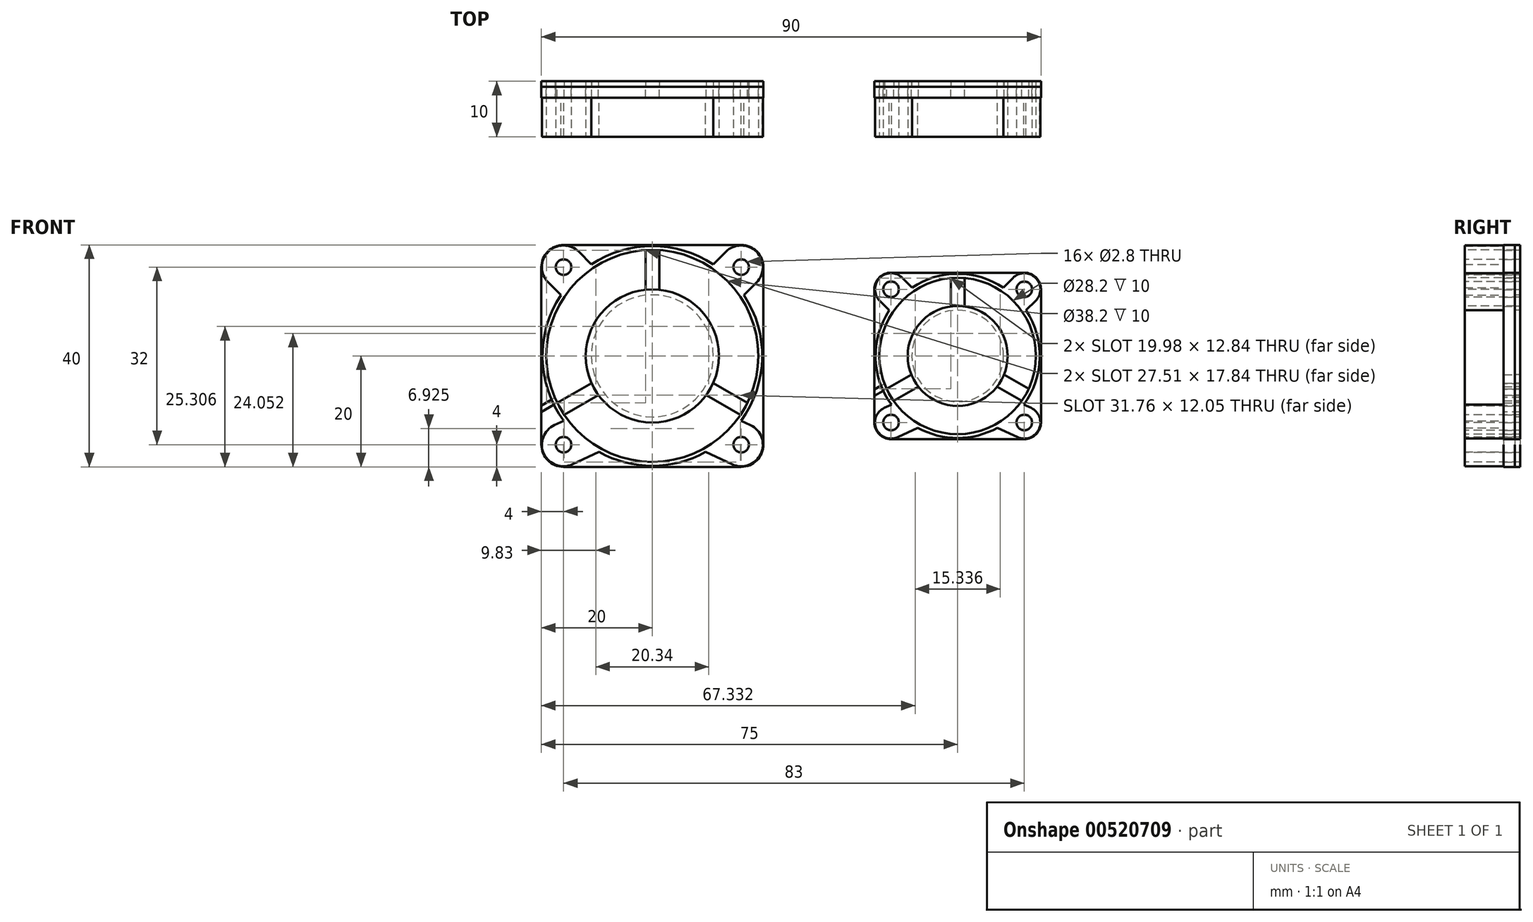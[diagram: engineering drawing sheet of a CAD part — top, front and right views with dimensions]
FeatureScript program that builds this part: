
annotation { "Feature Type Name" : "Feature", "Feature Type Description" : "" }
export const myFeature = defineFeature(function(context is Context, id is Id, definition is map)
    precondition{}
    {
        {
            assignVariable(context, id + "F0", {"name" : "height", "anyValue" : 10 * mm});
        }
        {
            assignVariable(context, id + "F1", {"name" : "lvl1_height", "anyValue" : 1 * mm});
        }
        {
            assignVariable(context, id + "F2", {"name" : "lvl2_height", "anyValue" : 2 * mm});
        }
        {
            var Q0;
            Q0=qCreatedBy(makeId("Front.planeOp"),FACE);
            var sketch = newSketch(context, id + "F3", { "sketchPlane" : qUnion([Q0])});
            skLineSegment(sketch, "E0", {"start": v(0, 0) * mm, "end": v(-30, 0) * mm, "construction": true});
            skLineSegment(sketch, "E1", {"start": v(0, 0) * mm, "end": v(25, 0) * mm, "construction": true});
            skCircle(sketch, "E2", {"center": v(-30, 0) * mm, "radius": 11 * mm});
            skCircle(sketch, "E3", {"center": v(25, 0) * mm, "radius": 8.25 * mm});
            skCircle(sketch, "E4", {"center": v(-30, 0) * mm, "radius": 12 * mm});
            skCircle(sketch, "E5", {"center": v(25, 0) * mm, "radius": 9 * mm});
            skCircle(sketch, "E6", {"center": v(-30, 0) * mm, "radius": 19.1 * mm});
            skCircle(sketch, "E7", {"center": v(25, 0) * mm, "radius": 14.1 * mm});
            skCircle(sketch, "E8", {"center": v(-30, 0) * mm, "radius": 19.8 * mm});
            skCircle(sketch, "E9", {"center": v(25, 0) * mm, "radius": 14.8 * mm});
            skLineSegment(sketch, "E10", {"start": v(-30, 0) * mm, "end": v(-28.75, 0) * mm, "construction": true});
            skLineSegment(sketch, "E11", {"start": v(-28.75, 0) * mm, "end": v(-28.75, 10.93) * mm, "construction": true});
            skLineSegment(sketch, "E12", {"start": v(-28.75, 10.93) * mm, "end": v(-28.75, 19.06) * mm});
            skLineSegment(sketch, "E13", {"start": v(-30, 0) * mm, "end": v(-30, 25) * mm, "construction": true});
            skLineSegment(sketch, "E14.MirrorCS", {"start": v(-31.25, 10.93) * mm, "end": v(-31.25, 19.06) * mm});
            skLineSegment(sketch, "E15.1.0", {"start": v(-40.09, -4.38) * mm, "end": v(-47.13, -8.45) * mm});
            skLineSegment(sketch, "E15.1.1", {"start": v(-38.84, -6.55) * mm, "end": v(-45.88, -10.61) * mm});
            skLineSegment(sketch, "E15.2.0", {"start": v(-21.16, -6.55) * mm, "end": v(-14.12, -10.61) * mm});
            skLineSegment(sketch, "E15.2.1", {"start": v(-19.91, -4.38) * mm, "end": v(-12.87, -8.45) * mm});
            skLineSegment(sketch, "E16", {"start": v(25, 0) * mm, "end": v(26.25, 0) * mm, "construction": true});
            skLineSegment(sketch, "E17", {"start": v(26.25, 0) * mm, "end": v(26.25, 8.15) * mm, "construction": true});
            skLineSegment(sketch, "E18", {"start": v(26.25, 8.15) * mm, "end": v(26.25, 14.04) * mm});
            skLineSegment(sketch, "E19", {"start": v(25, 0) * mm, "end": v(25, 20) * mm, "construction": true});
            skLineSegment(sketch, "E20.MirrorCS", {"start": v(23.75, 8.15) * mm, "end": v(23.75, 14.04) * mm});
            skLineSegment(sketch, "E21.1.0", {"start": v(17.31, -3) * mm, "end": v(12.21, -5.94) * mm});
            skLineSegment(sketch, "E21.1.1", {"start": v(18.56, -5.16) * mm, "end": v(13.46, -8.1) * mm});
            skLineSegment(sketch, "E21.2.0", {"start": v(31.44, -5.16) * mm, "end": v(36.54, -8.1) * mm});
            skLineSegment(sketch, "E21.2.1", {"start": v(32.69, -3) * mm, "end": v(37.79, -5.94) * mm});
            skLineSegment(sketch, "E22", {"start": v(-30, 0) * mm, "end": v(-46, 0) * mm, "construction": true});
            skLineSegment(sketch, "E23", {"start": v(-46, 0) * mm, "end": v(-46, 16) * mm, "construction": true});
            skCircle(sketch, "E24", {"center": v(-46, 16) * mm, "radius": 1.4 * mm});
            skCircle(sketch, "E25.1.0", {"center": v(-46, -16) * mm, "radius": 1.4 * mm});
            skCircle(sketch, "E25.2.0", {"center": v(-14, -16) * mm, "radius": 1.4 * mm});
            skCircle(sketch, "E25.3.0", {"center": v(-14, 16) * mm, "radius": 1.4 * mm});
            skLineSegment(sketch, "E26", {"start": v(25, 0) * mm, "end": v(13, 0) * mm, "construction": true});
            skLineSegment(sketch, "E27", {"start": v(13, 0) * mm, "end": v(13, 12) * mm, "construction": true});
            skCircle(sketch, "E28", {"center": v(13, 12) * mm, "radius": 1.4 * mm});
            skCircle(sketch, "E29.1.0", {"center": v(13, -12) * mm, "radius": 1.4 * mm});
            skCircle(sketch, "E29.2.0", {"center": v(37, -12) * mm, "radius": 1.4 * mm});
            skCircle(sketch, "E29.3.0", {"center": v(37, 12) * mm, "radius": 1.4 * mm});
            skLineSegment(sketch, "E30", {"start": v(-30, 20) * mm, "end": v(-46, 20) * mm});
            skLineSegment(sketch, "E31", {"start": v(-50, 16) * mm, "end": v(-50, 0) * mm});
            skPoint(sketch, "E32.visualSharp", {"position": v(-50, 20) * mm});
            skArc(sketch, "E32.filletArc", {"start": v(-46, 20) * mm, "mid": v(-48.83, 18.83) * mm, "end": v(-50, 16) * mm});
            skLineSegment(sketch, "E33.MirrorCS", {"start": v(-30, 20) * mm, "end": v(-14, 20) * mm});
            skLineSegment(sketch, "E34.MirrorCS", {"start": v(-10, 16) * mm, "end": v(-10, 0) * mm});
            skArc(sketch, "E35.MirrorCS", {"start": v(-14, 20) * mm, "mid": v(-11.17, 18.83) * mm, "end": v(-10, 16) * mm});
            skLineSegment(sketch, "E36.MirrorCS", {"start": v(-50, -16) * mm, "end": v(-50, 0) * mm});
            skArc(sketch, "E37.MirrorCS", {"start": v(-46, -20) * mm, "mid": v(-48.83, -18.83) * mm, "end": v(-50, -16) * mm});
            skLineSegment(sketch, "E38.MirrorCS", {"start": v(-30, -20) * mm, "end": v(-46, -20) * mm});
            skLineSegment(sketch, "E39.MirrorCS", {"start": v(-10, -16) * mm, "end": v(-10, 0) * mm});
            skLineSegment(sketch, "E40.MirrorCS", {"start": v(-30, -20) * mm, "end": v(-14, -20) * mm});
            skArc(sketch, "E41.MirrorCS", {"start": v(-14, -20) * mm, "mid": v(-11.17, -18.83) * mm, "end": v(-10, -16) * mm});
            skLineSegment(sketch, "E42", {"start": v(25, 15) * mm, "end": v(13, 15) * mm});
            skLineSegment(sketch, "E43", {"start": v(10, 12) * mm, "end": v(10, 0) * mm});
            skPoint(sketch, "E44.visualSharp", {"position": v(10, 15) * mm});
            skArc(sketch, "E44.filletArc", {"start": v(13, 15) * mm, "mid": v(10.88, 14.12) * mm, "end": v(10, 12) * mm});
            skLineSegment(sketch, "E45.MirrorCS", {"start": v(25, 15) * mm, "end": v(37, 15) * mm});
            skLineSegment(sketch, "E46.MirrorCS", {"start": v(40, 12) * mm, "end": v(40, 0) * mm});
            skArc(sketch, "E47.MirrorCS", {"start": v(37, 15) * mm, "mid": v(39.12, 14.12) * mm, "end": v(40, 12) * mm});
            skLineSegment(sketch, "E48.MirrorCS", {"start": v(10, -12) * mm, "end": v(10, 0) * mm});
            skArc(sketch, "E49.MirrorCS", {"start": v(13, -15) * mm, "mid": v(10.88, -14.12) * mm, "end": v(10, -12) * mm});
            skLineSegment(sketch, "E50.MirrorCS", {"start": v(25, -15) * mm, "end": v(13, -15) * mm});
            skLineSegment(sketch, "E51.MirrorCS", {"start": v(40, -12) * mm, "end": v(40, 0) * mm});
            skLineSegment(sketch, "E52.MirrorCS", {"start": v(25, -15) * mm, "end": v(37, -15) * mm});
            skArc(sketch, "E53.MirrorCS", {"start": v(37, -15) * mm, "mid": v(39.12, -14.12) * mm, "end": v(40, -12) * mm});
            skLineSegment(sketch, "E54", {"start": v(-40.97, 16.48) * mm, "end": v(-43.24, 18.76) * mm});
            skLineSegment(sketch, "E55", {"start": v(-46.48, 10.97) * mm, "end": v(-48.76, 13.24) * mm});
            skArc(sketch, "E56", {"start": v(-43.24, 18.76) * mm, "mid": v(-48.76, 18.76) * mm, "end": v(-48.76, 13.24) * mm});
            skLineSegment(sketch, "E57.MirrorCS", {"start": v(-19.03, 16.48) * mm, "end": v(-16.76, 18.76) * mm});
            skLineSegment(sketch, "E58.MirrorCS", {"start": v(-13.52, 10.97) * mm, "end": v(-11.24, 13.24) * mm});
            skArc(sketch, "E59.MirrorCS", {"start": v(-16.76, 18.76) * mm, "mid": v(-11.24, 18.76) * mm, "end": v(-11.24, 13.24) * mm});
            skLineSegment(sketch, "E60", {"start": v(-47.7, -12.37) * mm, "end": v(-46, -16) * mm, "construction": true});
            skLineSegment(sketch, "E61", {"start": v(-46, -16) * mm, "end": v(-44.13, -20) * mm, "construction": true});
            skArc(sketch, "E62", {"start": v(-44.35, -19.53) * mm, "mid": v(-49.53, -17.65) * mm, "end": v(-47.65, -12.47) * mm});
            skLineSegment(sketch, "E63", {"start": v(-44.35, -19.53) * mm, "end": v(-39.6, -17.32) * mm});
            skLineSegment(sketch, "E64", {"start": v(-47.65, -12.47) * mm, "end": v(-45.98, -11.69) * mm});
            skLineSegment(sketch, "E65.MirrorCS", {"start": v(-12.35, -12.47) * mm, "end": v(-14.02, -11.69) * mm});
            skLineSegment(sketch, "E66.MirrorCS", {"start": v(-15.65, -19.53) * mm, "end": v(-20.4, -17.32) * mm});
            skArc(sketch, "E67.MirrorCS", {"start": v(-15.65, -19.53) * mm, "mid": v(-10.47, -17.65) * mm, "end": v(-12.35, -12.47) * mm});
            skLineSegment(sketch, "E68", {"start": v(-47.13, -8.45) * mm, "end": v(-50, -10.1) * mm});
            skLineSegment(sketch, "E69", {"start": v(-47.55, -7.53) * mm, "end": v(-50, -8.95) * mm});
            skLineSegment(sketch, "E70", {"start": v(15.12, 14.12) * mm, "end": v(13, 12) * mm, "construction": true});
            skLineSegment(sketch, "E71", {"start": v(13, 12) * mm, "end": v(10.88, 9.88) * mm, "construction": true});
            skArc(sketch, "E72", {"start": v(15.05, 14.05) * mm, "mid": v(10.95, 14.05) * mm, "end": v(10.95, 9.95) * mm});
            skLineSegment(sketch, "E73", {"start": v(15.05, 14.05) * mm, "end": v(16.79, 12.31) * mm});
            skLineSegment(sketch, "E74", {"start": v(10.95, 9.95) * mm, "end": v(12.69, 8.21) * mm});
            skLineSegment(sketch, "E75", {"start": v(11.73, -9.28) * mm, "end": v(13, -12) * mm, "construction": true});
            skLineSegment(sketch, "E76", {"start": v(13, -12) * mm, "end": v(14.27, -14.72) * mm, "construction": true});
            skArc(sketch, "E77", {"start": v(11.77, -9.37) * mm, "mid": v(10.37, -13.23) * mm, "end": v(14.23, -14.63) * mm});
            skLineSegment(sketch, "E78", {"start": v(11.77, -9.37) * mm, "end": v(13.07, -8.77) * mm});
            skLineSegment(sketch, "E79", {"start": v(14.23, -14.63) * mm, "end": v(17.83, -12.95) * mm});
            skArc(sketch, "E80.MirrorCS", {"start": v(38.23, -9.37) * mm, "mid": v(39.63, -13.23) * mm, "end": v(35.77, -14.63) * mm});
            skLineSegment(sketch, "E81.MirrorCS", {"start": v(35.77, -14.63) * mm, "end": v(32.17, -12.95) * mm});
            skLineSegment(sketch, "E82.MirrorCS", {"start": v(38.23, -9.37) * mm, "end": v(36.93, -8.77) * mm});
            skLineSegment(sketch, "E83.MirrorCS", {"start": v(34.95, 14.05) * mm, "end": v(33.21, 12.31) * mm});
            skLineSegment(sketch, "E84.MirrorCS", {"start": v(39.05, 9.95) * mm, "end": v(37.31, 8.21) * mm});
            skArc(sketch, "E85.MirrorCS", {"start": v(34.95, 14.05) * mm, "mid": v(39.05, 14.05) * mm, "end": v(39.05, 9.95) * mm});
            skLineSegment(sketch, "E86", {"start": v(12.21, -5.94) * mm, "end": v(10, -7.22) * mm});
            skLineSegment(sketch, "E87", {"start": v(11.82, -5.01) * mm, "end": v(10, -6.06) * mm});
            skSolve(sketch);
        }
        {
            var Q0;
            Q0=makeQuery(id+"F3.imprint","IMPRINT",FACE,{"disambiguationData":[TD([[makeQuery(id+"F3.imprint","IMPRINT",EDGE,{"derivedFrom":sQuery(id+"F3.wireOp",EDGE,"E25.3.0")}),-1.0]])]});
            var Q1;
            Q1=makeQuery(id+"F3.imprint","IMPRINT",FACE,{"disambiguationData":[TD([[makeQuery(id+"F3.imprint","IMPRINT",EDGE,{"derivedFrom":sQuery(id+"F3.wireOp",EDGE,"E30")}),1.0]])]});
            var Q2;
            {var subQ4=sQuery(id+"F3.wireOp",EDGE,"E6");var subQ5=makeQuery(id+"F3.imprint","INTERSECT",VERTEX,{"derivedFrom":[subQ4,sQuery(id+"F3.wireOp",EDGE,"E12")]});Q2=makeQuery(id+"F3.imprint","IMPRINT",FACE,{"disambiguationData":[TD([[makeQuery(id+"F3.imprint","IMPRINT",EDGE,{"disambiguationData":[TD([[subQ5,-1.0]])],"derivedFrom":subQ4}),-1.0]])]});}
            var Q3;
            Q3=makeQuery(id+"F3.imprint","IMPRINT",FACE,{"disambiguationData":[TD([[makeQuery(id+"F3.imprint","IMPRINT",EDGE,{"derivedFrom":sQuery(id+"F3.wireOp",EDGE,"E24")}),-1.0]])]});
            var Q4;
            Q4=makeQuery(id+"F3.imprint","IMPRINT",FACE,{"disambiguationData":[TD([[makeQuery(id+"F3.imprint","IMPRINT",EDGE,{"derivedFrom":sQuery(id+"F3.wireOp",EDGE,"E25.1.0")}),-1.0]])]});
            var Q5;
            Q5=makeQuery(id+"F3.imprint","IMPRINT",FACE,{"disambiguationData":[TD([[makeQuery(id+"F3.imprint","IMPRINT",EDGE,{"derivedFrom":sQuery(id+"F3.wireOp",EDGE,"E25.2.0")}),-1.0]])]});
            var Q6;
            Q6=makeQuery(id+"F3.imprint","IMPRINT",FACE,{"disambiguationData":[TD([[makeQuery(id+"F3.imprint","IMPRINT",EDGE,{"derivedFrom":sQuery(id+"F3.wireOp",EDGE,"E29.2.0")}),-1.0]])]});
            var Q7;
            Q7=makeQuery(id+"F3.imprint","IMPRINT",FACE,{"disambiguationData":[TD([[makeQuery(id+"F3.imprint","IMPRINT",EDGE,{"derivedFrom":sQuery(id+"F3.wireOp",EDGE,"E42")}),1.0]])]});
            var Q8;
            Q8=makeQuery(id+"F3.imprint","IMPRINT",FACE,{"disambiguationData":[TD([[makeQuery(id+"F3.imprint","IMPRINT",EDGE,{"derivedFrom":sQuery(id+"F3.wireOp",EDGE,"E29.1.0")}),-1.0]])]});
            var Q9;
            Q9=makeQuery(id+"F3.imprint","IMPRINT",FACE,{"disambiguationData":[TD([[makeQuery(id+"F3.imprint","IMPRINT",EDGE,{"derivedFrom":sQuery(id+"F3.wireOp",EDGE,"E28")}),-1.0]])]});
            var Q10;
            Q10=makeQuery(id+"F3.imprint","IMPRINT",FACE,{"disambiguationData":[TD([[makeQuery(id+"F3.imprint","IMPRINT",EDGE,{"derivedFrom":sQuery(id+"F3.wireOp",EDGE,"E29.3.0")}),-1.0]])]});
            var Q11;
            {var subQ7=sQuery(id+"F3.wireOp",EDGE,"E7");var subQ8=makeQuery(id+"F3.imprint","INTERSECT",VERTEX,{"derivedFrom":[subQ7,sQuery(id+"F3.wireOp",EDGE,"E18")]});Q11=makeQuery(id+"F3.imprint","IMPRINT",FACE,{"disambiguationData":[TD([[makeQuery(id+"F3.imprint","IMPRINT",EDGE,{"disambiguationData":[TD([[subQ8,-1.0]])],"derivedFrom":subQ7}),-1.0]])]});}
            var Q12;
            {var subQ0=sQuery(id+"F3.wireOp",EDGE,"E15.2.0");var subQ1=sQuery(id+"F3.wireOp",EDGE,"E4");var subQ2=makeQuery(id+"F3.imprint","INTERSECT",VERTEX,{"derivedFrom":[subQ1,subQ0]});Q12=makeQuery(id+"F3.imprint","IMPRINT",FACE,{"disambiguationData":[TD([[makeQuery(id+"F3.imprint","IMPRINT",EDGE,{"disambiguationData":[TD([[subQ2,-1.0]])],"derivedFrom":subQ1}),-1.0]])]});}
            var Q13;
            {var subQ0=sQuery(id+"F3.wireOp",EDGE,"E15.1.0");var subQ1=sQuery(id+"F3.wireOp",EDGE,"E4");var subQ2=makeQuery(id+"F3.imprint","INTERSECT",VERTEX,{"derivedFrom":[subQ1,subQ0]});Q13=makeQuery(id+"F3.imprint","IMPRINT",FACE,{"disambiguationData":[TD([[makeQuery(id+"F3.imprint","IMPRINT",EDGE,{"disambiguationData":[TD([[subQ2,-1.0]])],"derivedFrom":subQ1}),-1.0]])]});}
            var Q14;
            {var subQ0=sQuery(id+"F3.wireOp",EDGE,"E14.MirrorCS");var subQ1=sQuery(id+"F3.wireOp",EDGE,"E4");var subQ2=makeQuery(id+"F3.imprint","INTERSECT",VERTEX,{"derivedFrom":[subQ1,subQ0]});Q14=makeQuery(id+"F3.imprint","IMPRINT",FACE,{"disambiguationData":[TD([[makeQuery(id+"F3.imprint","IMPRINT",EDGE,{"disambiguationData":[TD([[subQ2,1.0]])],"derivedFrom":subQ1}),-1.0]])]});}
            var Q15;
            {var subQ0=sQuery(id+"F3.wireOp",EDGE,"E12");var subQ1=sQuery(id+"F3.wireOp",EDGE,"E2");var subQ2=makeQuery(id+"F3.imprint","INTERSECT",VERTEX,{"derivedFrom":[subQ1,subQ0]});Q15=makeQuery(id+"F3.imprint","IMPRINT",FACE,{"disambiguationData":[TD([[makeQuery(id+"F3.imprint","IMPRINT",EDGE,{"disambiguationData":[TD([[subQ2,1.0]])],"derivedFrom":subQ1}),-1.0]])]});}
            var Q16;
            {var subQ0=sQuery(id+"F3.wireOp",EDGE,"E15.2.0");var subQ1=sQuery(id+"F3.wireOp",EDGE,"E2");var subQ2=makeQuery(id+"F3.imprint","INTERSECT",VERTEX,{"derivedFrom":[subQ1,subQ0]});Q16=makeQuery(id+"F3.imprint","IMPRINT",FACE,{"disambiguationData":[TD([[makeQuery(id+"F3.imprint","IMPRINT",EDGE,{"disambiguationData":[TD([[subQ2,-1.0]])],"derivedFrom":subQ1}),-1.0]])]});}
            var Q17;
            {var subQ0=sQuery(id+"F3.wireOp",EDGE,"E15.1.1");var subQ1=sQuery(id+"F3.wireOp",EDGE,"E2");var subQ2=makeQuery(id+"F3.imprint","INTERSECT",VERTEX,{"derivedFrom":[subQ1,subQ0]});Q17=makeQuery(id+"F3.imprint","IMPRINT",FACE,{"disambiguationData":[TD([[makeQuery(id+"F3.imprint","IMPRINT",EDGE,{"disambiguationData":[TD([[subQ2,-1.0]])],"derivedFrom":subQ1}),-1.0]])]});}
            var Q18;
            {var subQ0=sQuery(id+"F3.wireOp",EDGE,"E14.MirrorCS");var subQ1=sQuery(id+"F3.wireOp",EDGE,"E2");var subQ2=makeQuery(id+"F3.imprint","INTERSECT",VERTEX,{"derivedFrom":[subQ1,subQ0]});Q18=makeQuery(id+"F3.imprint","IMPRINT",FACE,{"disambiguationData":[TD([[makeQuery(id+"F3.imprint","IMPRINT",EDGE,{"disambiguationData":[TD([[subQ2,-1.0]])],"derivedFrom":subQ1}),-1.0]])]});}
            var Q19;
            {var subQ0=sQuery(id+"F3.wireOp",EDGE,"E15.1.0");var subQ1=sQuery(id+"F3.wireOp",EDGE,"E2");var subQ2=makeQuery(id+"F3.imprint","INTERSECT",VERTEX,{"derivedFrom":[subQ1,subQ0]});Q19=makeQuery(id+"F3.imprint","IMPRINT",FACE,{"disambiguationData":[TD([[makeQuery(id+"F3.imprint","IMPRINT",EDGE,{"disambiguationData":[TD([[subQ2,-1.0]])],"derivedFrom":subQ1}),-1.0]])]});}
            var Q20;
            {var subQ0=sQuery(id+"F3.wireOp",EDGE,"E12");var subQ1=sQuery(id+"F3.wireOp",EDGE,"E2");var subQ2=makeQuery(id+"F3.imprint","INTERSECT",VERTEX,{"derivedFrom":[subQ1,subQ0]});Q20=makeQuery(id+"F3.imprint","IMPRINT",FACE,{"disambiguationData":[TD([[makeQuery(id+"F3.imprint","IMPRINT",EDGE,{"disambiguationData":[TD([[subQ2,-1.0]])],"derivedFrom":subQ1}),-1.0]])]});}
            var Q21;
            {var subQ0=sQuery(id+"F3.wireOp",EDGE,"E21.2.0");var subQ1=sQuery(id+"F3.wireOp",EDGE,"E5");var subQ2=makeQuery(id+"F3.imprint","INTERSECT",VERTEX,{"derivedFrom":[subQ1,subQ0]});Q21=makeQuery(id+"F3.imprint","IMPRINT",FACE,{"disambiguationData":[TD([[makeQuery(id+"F3.imprint","IMPRINT",EDGE,{"disambiguationData":[TD([[subQ2,-1.0]])],"derivedFrom":subQ1}),-1.0]])]});}
            var Q22;
            {var subQ0=sQuery(id+"F3.wireOp",EDGE,"E21.1.0");var subQ1=sQuery(id+"F3.wireOp",EDGE,"E5");var subQ2=makeQuery(id+"F3.imprint","INTERSECT",VERTEX,{"derivedFrom":[subQ1,subQ0]});Q22=makeQuery(id+"F3.imprint","IMPRINT",FACE,{"disambiguationData":[TD([[makeQuery(id+"F3.imprint","IMPRINT",EDGE,{"disambiguationData":[TD([[subQ2,-1.0]])],"derivedFrom":subQ1}),-1.0]])]});}
            var Q23;
            {var subQ0=sQuery(id+"F3.wireOp",EDGE,"E18");var subQ1=sQuery(id+"F3.wireOp",EDGE,"E3");var subQ2=makeQuery(id+"F3.imprint","INTERSECT",VERTEX,{"derivedFrom":[subQ1,subQ0]});Q23=makeQuery(id+"F3.imprint","IMPRINT",FACE,{"disambiguationData":[TD([[makeQuery(id+"F3.imprint","IMPRINT",EDGE,{"disambiguationData":[TD([[subQ2,1.0]])],"derivedFrom":subQ1}),-1.0]])]});}
            var Q24;
            {var subQ0=sQuery(id+"F3.wireOp",EDGE,"E21.2.0");var subQ1=sQuery(id+"F3.wireOp",EDGE,"E3");var subQ2=makeQuery(id+"F3.imprint","INTERSECT",VERTEX,{"derivedFrom":[subQ1,subQ0]});Q24=makeQuery(id+"F3.imprint","IMPRINT",FACE,{"disambiguationData":[TD([[makeQuery(id+"F3.imprint","IMPRINT",EDGE,{"disambiguationData":[TD([[subQ2,-1.0]])],"derivedFrom":subQ1}),-1.0]])]});}
            var Q25;
            {var subQ0=sQuery(id+"F3.wireOp",EDGE,"E21.1.1");var subQ1=sQuery(id+"F3.wireOp",EDGE,"E3");var subQ2=makeQuery(id+"F3.imprint","INTERSECT",VERTEX,{"derivedFrom":[subQ1,subQ0]});Q25=makeQuery(id+"F3.imprint","IMPRINT",FACE,{"disambiguationData":[TD([[makeQuery(id+"F3.imprint","IMPRINT",EDGE,{"disambiguationData":[TD([[subQ2,-1.0]])],"derivedFrom":subQ1}),-1.0]])]});}
            var Q26;
            {var subQ0=sQuery(id+"F3.wireOp",EDGE,"E20.MirrorCS");var subQ1=sQuery(id+"F3.wireOp",EDGE,"E3");var subQ2=makeQuery(id+"F3.imprint","INTERSECT",VERTEX,{"derivedFrom":[subQ1,subQ0]});Q26=makeQuery(id+"F3.imprint","IMPRINT",FACE,{"disambiguationData":[TD([[makeQuery(id+"F3.imprint","IMPRINT",EDGE,{"disambiguationData":[TD([[subQ2,-1.0]])],"derivedFrom":subQ1}),-1.0]])]});}
            var Q27;
            {var subQ0=sQuery(id+"F3.wireOp",EDGE,"E21.1.0");var subQ1=sQuery(id+"F3.wireOp",EDGE,"E3");var subQ2=makeQuery(id+"F3.imprint","INTERSECT",VERTEX,{"derivedFrom":[subQ1,subQ0]});Q27=makeQuery(id+"F3.imprint","IMPRINT",FACE,{"disambiguationData":[TD([[makeQuery(id+"F3.imprint","IMPRINT",EDGE,{"disambiguationData":[TD([[subQ2,-1.0]])],"derivedFrom":subQ1}),-1.0]])]});}
            var Q28;
            {var subQ0=sQuery(id+"F3.wireOp",EDGE,"E18");var subQ1=sQuery(id+"F3.wireOp",EDGE,"E3");var subQ2=makeQuery(id+"F3.imprint","INTERSECT",VERTEX,{"derivedFrom":[subQ1,subQ0]});Q28=makeQuery(id+"F3.imprint","IMPRINT",FACE,{"disambiguationData":[TD([[makeQuery(id+"F3.imprint","IMPRINT",EDGE,{"disambiguationData":[TD([[subQ2,-1.0]])],"derivedFrom":subQ1}),-1.0]])]});}
            var Q29;
            {var subQ0=sQuery(id+"F3.wireOp",EDGE,"E20.MirrorCS");var subQ1=sQuery(id+"F3.wireOp",EDGE,"E5");var subQ2=makeQuery(id+"F3.imprint","INTERSECT",VERTEX,{"derivedFrom":[subQ1,subQ0]});Q29=makeQuery(id+"F3.imprint","IMPRINT",FACE,{"disambiguationData":[TD([[makeQuery(id+"F3.imprint","IMPRINT",EDGE,{"disambiguationData":[TD([[subQ2,1.0]])],"derivedFrom":subQ1}),-1.0]])]});}
            extrude(context, id + "F4", {"entities" : qUnion([Q0, Q1, Q2, Q3, Q4, Q5, Q6, Q7, Q8, Q9, Q10, Q11, Q12, Q13, Q14, Q15, Q16, Q17, Q18, Q19, Q20, Q21, Q22, Q23, Q24, Q25, Q26, Q27, Q28, Q29]), "oppositeDirection" : true, "depth" : getVariable(context, 'lvl1_height'), "offsetDistance" : 25 * mm});
        }
        {
            var Q0;
            Q0=makeQuery(id+"F3.imprint","IMPRINT",FACE,{"disambiguationData":[TD([[makeQuery(id+"F3.imprint","IMPRINT",EDGE,{"derivedFrom":sQuery(id+"F3.wireOp",EDGE,"E30")}),1.0]])]});
            var Q1;
            Q1=makeQuery(id+"F3.imprint","IMPRINT",FACE,{"disambiguationData":[TD([[makeQuery(id+"F3.imprint","IMPRINT",EDGE,{"derivedFrom":sQuery(id+"F3.wireOp",EDGE,"E42")}),1.0]])]});
            extrude(context, id + "F5", {"entities" : qUnion([Q0, Q1]), "operationType" : NewBodyOperationType.ADD, "depth" : getVariable(context, 'lvl2_height'), "offsetDistance" : 25 * mm});
        }
        {
            var Q0;
            {var subQ7=sQuery(id+"F3.wireOp",EDGE,"E7");var subQ8=makeQuery(id+"F3.imprint","INTERSECT",VERTEX,{"derivedFrom":[subQ7,sQuery(id+"F3.wireOp",EDGE,"E18")]});Q0=makeQuery(id+"F3.imprint","IMPRINT",FACE,{"disambiguationData":[TD([[makeQuery(id+"F3.imprint","IMPRINT",EDGE,{"disambiguationData":[TD([[subQ8,-1.0]])],"derivedFrom":subQ7}),-1.0]])]});}
            var Q1;
            Q1=makeQuery(id+"F3.imprint","IMPRINT",FACE,{"disambiguationData":[TD([[makeQuery(id+"F3.imprint","IMPRINT",EDGE,{"derivedFrom":sQuery(id+"F3.wireOp",EDGE,"E29.3.0")}),-1.0]])]});
            var Q2;
            {var subQ3=sQuery(id+"F3.wireOp",EDGE,"E87");var subQ5=sQuery(id+"F3.wireOp",EDGE,"E9");var subQ6=makeQuery(id+"F3.imprint","INTERSECT",VERTEX,{"derivedFrom":[subQ5,subQ3]});Q2=makeQuery(id+"F3.imprint","IMPRINT",FACE,{"disambiguationData":[TD([[makeQuery(id+"F3.imprint","IMPRINT",EDGE,{"disambiguationData":[TD([[subQ6,-1.0]])],"derivedFrom":subQ5}),1.0]])]});}
            var Q3;
            {var subQ0=sQuery(id+"F3.wireOp",EDGE,"E3");var subQ5=makeQuery(id+"F3.imprint","INTERSECT",VERTEX,{"derivedFrom":[subQ0,sQuery(id+"F3.wireOp",EDGE,"E18")]});Q3=makeQuery(id+"F3.imprint","IMPRINT",FACE,{"disambiguationData":[TD([[makeQuery(id+"F3.imprint","IMPRINT",EDGE,{"disambiguationData":[TD([[subQ5,-1.0]])],"derivedFrom":subQ0}),1.0]])]});}
            var Q4;
            {var subQ0=sQuery(id+"F3.wireOp",EDGE,"E20.MirrorCS");var subQ1=sQuery(id+"F3.wireOp",EDGE,"E3");var subQ2=makeQuery(id+"F3.imprint","INTERSECT",VERTEX,{"derivedFrom":[subQ1,subQ0]});Q4=makeQuery(id+"F3.imprint","IMPRINT",FACE,{"disambiguationData":[TD([[makeQuery(id+"F3.imprint","IMPRINT",EDGE,{"disambiguationData":[TD([[subQ2,-1.0]])],"derivedFrom":subQ1}),-1.0]])]});}
            var Q5;
            {var subQ0=sQuery(id+"F3.wireOp",EDGE,"E18");var subQ1=sQuery(id+"F3.wireOp",EDGE,"E3");var subQ2=makeQuery(id+"F3.imprint","INTERSECT",VERTEX,{"derivedFrom":[subQ1,subQ0]});Q5=makeQuery(id+"F3.imprint","IMPRINT",FACE,{"disambiguationData":[TD([[makeQuery(id+"F3.imprint","IMPRINT",EDGE,{"disambiguationData":[TD([[subQ2,1.0]])],"derivedFrom":subQ1}),-1.0]])]});}
            var Q6;
            {var subQ0=sQuery(id+"F3.wireOp",EDGE,"E18");var subQ1=sQuery(id+"F3.wireOp",EDGE,"E3");var subQ2=makeQuery(id+"F3.imprint","INTERSECT",VERTEX,{"derivedFrom":[subQ1,subQ0]});Q6=makeQuery(id+"F3.imprint","IMPRINT",FACE,{"disambiguationData":[TD([[makeQuery(id+"F3.imprint","IMPRINT",EDGE,{"disambiguationData":[TD([[subQ2,-1.0]])],"derivedFrom":subQ1}),-1.0]])]});}
            var Q7;
            {var subQ0=sQuery(id+"F3.wireOp",EDGE,"E21.2.0");var subQ1=sQuery(id+"F3.wireOp",EDGE,"E3");var subQ2=makeQuery(id+"F3.imprint","INTERSECT",VERTEX,{"derivedFrom":[subQ1,subQ0]});Q7=makeQuery(id+"F3.imprint","IMPRINT",FACE,{"disambiguationData":[TD([[makeQuery(id+"F3.imprint","IMPRINT",EDGE,{"disambiguationData":[TD([[subQ2,-1.0]])],"derivedFrom":subQ1}),-1.0]])]});}
            var Q8;
            {var subQ0=sQuery(id+"F3.wireOp",EDGE,"E21.1.0");var subQ1=sQuery(id+"F3.wireOp",EDGE,"E3");var subQ2=makeQuery(id+"F3.imprint","INTERSECT",VERTEX,{"derivedFrom":[subQ1,subQ0]});Q8=makeQuery(id+"F3.imprint","IMPRINT",FACE,{"disambiguationData":[TD([[makeQuery(id+"F3.imprint","IMPRINT",EDGE,{"disambiguationData":[TD([[subQ2,-1.0]])],"derivedFrom":subQ1}),-1.0]])]});}
            var Q9;
            {var subQ0=sQuery(id+"F3.wireOp",EDGE,"E21.1.1");var subQ1=sQuery(id+"F3.wireOp",EDGE,"E3");var subQ2=makeQuery(id+"F3.imprint","INTERSECT",VERTEX,{"derivedFrom":[subQ1,subQ0]});Q9=makeQuery(id+"F3.imprint","IMPRINT",FACE,{"disambiguationData":[TD([[makeQuery(id+"F3.imprint","IMPRINT",EDGE,{"disambiguationData":[TD([[subQ2,-1.0]])],"derivedFrom":subQ1}),-1.0]])]});}
            var Q10;
            Q10=makeQuery(id+"F3.imprint","IMPRINT",FACE,{"disambiguationData":[TD([[makeQuery(id+"F3.imprint","IMPRINT",EDGE,{"derivedFrom":sQuery(id+"F3.wireOp",EDGE,"E29.2.0")}),-1.0]])]});
            var Q11;
            Q11=makeQuery(id+"F3.imprint","IMPRINT",FACE,{"disambiguationData":[TD([[makeQuery(id+"F3.imprint","IMPRINT",EDGE,{"derivedFrom":sQuery(id+"F3.wireOp",EDGE,"E29.1.0")}),-1.0]])]});
            var Q12;
            Q12=makeQuery(id+"F3.imprint","IMPRINT",FACE,{"disambiguationData":[TD([[makeQuery(id+"F3.imprint","IMPRINT",EDGE,{"derivedFrom":sQuery(id+"F3.wireOp",EDGE,"E28")}),-1.0]])]});
            var Q13;
            Q13=makeQuery(id+"F3.imprint","IMPRINT",FACE,{"disambiguationData":[TD([[makeQuery(id+"F3.imprint","IMPRINT",EDGE,{"derivedFrom":sQuery(id+"F3.wireOp",EDGE,"E25.3.0")}),-1.0]])]});
            var Q14;
            Q14=makeQuery(id+"F3.imprint","IMPRINT",FACE,{"disambiguationData":[TD([[makeQuery(id+"F3.imprint","IMPRINT",EDGE,{"derivedFrom":sQuery(id+"F3.wireOp",EDGE,"E25.2.0")}),-1.0]])]});
            var Q15;
            Q15=makeQuery(id+"F3.imprint","IMPRINT",FACE,{"disambiguationData":[TD([[makeQuery(id+"F3.imprint","IMPRINT",EDGE,{"derivedFrom":sQuery(id+"F3.wireOp",EDGE,"E25.1.0")}),-1.0]])]});
            var Q16;
            Q16=makeQuery(id+"F3.imprint","IMPRINT",FACE,{"disambiguationData":[TD([[makeQuery(id+"F3.imprint","IMPRINT",EDGE,{"derivedFrom":sQuery(id+"F3.wireOp",EDGE,"E24")}),-1.0]])]});
            var Q17;
            {var subQ0=sQuery(id+"F3.wireOp",EDGE,"E2");var subQ5=makeQuery(id+"F3.imprint","INTERSECT",VERTEX,{"derivedFrom":[subQ0,sQuery(id+"F3.wireOp",EDGE,"E12")]});Q17=makeQuery(id+"F3.imprint","IMPRINT",FACE,{"disambiguationData":[TD([[makeQuery(id+"F3.imprint","IMPRINT",EDGE,{"disambiguationData":[TD([[subQ5,-1.0]])],"derivedFrom":subQ0}),1.0]])]});}
            var Q18;
            {var subQ4=sQuery(id+"F3.wireOp",EDGE,"E6");var subQ5=makeQuery(id+"F3.imprint","INTERSECT",VERTEX,{"derivedFrom":[subQ4,sQuery(id+"F3.wireOp",EDGE,"E12")]});Q18=makeQuery(id+"F3.imprint","IMPRINT",FACE,{"disambiguationData":[TD([[makeQuery(id+"F3.imprint","IMPRINT",EDGE,{"disambiguationData":[TD([[subQ5,-1.0]])],"derivedFrom":subQ4}),-1.0]])]});}
            var Q19;
            {var subQ0=sQuery(id+"F3.wireOp",EDGE,"E12");var subQ1=sQuery(id+"F3.wireOp",EDGE,"E2");var subQ2=makeQuery(id+"F3.imprint","INTERSECT",VERTEX,{"derivedFrom":[subQ1,subQ0]});Q19=makeQuery(id+"F3.imprint","IMPRINT",FACE,{"disambiguationData":[TD([[makeQuery(id+"F3.imprint","IMPRINT",EDGE,{"disambiguationData":[TD([[subQ2,1.0]])],"derivedFrom":subQ1}),-1.0]])]});}
            var Q20;
            {var subQ0=sQuery(id+"F3.wireOp",EDGE,"E12");var subQ1=sQuery(id+"F3.wireOp",EDGE,"E2");var subQ2=makeQuery(id+"F3.imprint","INTERSECT",VERTEX,{"derivedFrom":[subQ1,subQ0]});Q20=makeQuery(id+"F3.imprint","IMPRINT",FACE,{"disambiguationData":[TD([[makeQuery(id+"F3.imprint","IMPRINT",EDGE,{"disambiguationData":[TD([[subQ2,-1.0]])],"derivedFrom":subQ1}),-1.0]])]});}
            var Q21;
            {var subQ0=sQuery(id+"F3.wireOp",EDGE,"E14.MirrorCS");var subQ1=sQuery(id+"F3.wireOp",EDGE,"E2");var subQ2=makeQuery(id+"F3.imprint","INTERSECT",VERTEX,{"derivedFrom":[subQ1,subQ0]});Q21=makeQuery(id+"F3.imprint","IMPRINT",FACE,{"disambiguationData":[TD([[makeQuery(id+"F3.imprint","IMPRINT",EDGE,{"disambiguationData":[TD([[subQ2,-1.0]])],"derivedFrom":subQ1}),-1.0]])]});}
            var Q22;
            {var subQ0=sQuery(id+"F3.wireOp",EDGE,"E15.1.0");var subQ1=sQuery(id+"F3.wireOp",EDGE,"E2");var subQ2=makeQuery(id+"F3.imprint","INTERSECT",VERTEX,{"derivedFrom":[subQ1,subQ0]});Q22=makeQuery(id+"F3.imprint","IMPRINT",FACE,{"disambiguationData":[TD([[makeQuery(id+"F3.imprint","IMPRINT",EDGE,{"disambiguationData":[TD([[subQ2,-1.0]])],"derivedFrom":subQ1}),-1.0]])]});}
            var Q23;
            {var subQ0=sQuery(id+"F3.wireOp",EDGE,"E15.1.1");var subQ1=sQuery(id+"F3.wireOp",EDGE,"E2");var subQ2=makeQuery(id+"F3.imprint","INTERSECT",VERTEX,{"derivedFrom":[subQ1,subQ0]});Q23=makeQuery(id+"F3.imprint","IMPRINT",FACE,{"disambiguationData":[TD([[makeQuery(id+"F3.imprint","IMPRINT",EDGE,{"disambiguationData":[TD([[subQ2,-1.0]])],"derivedFrom":subQ1}),-1.0]])]});}
            var Q24;
            {var subQ0=sQuery(id+"F3.wireOp",EDGE,"E15.2.0");var subQ1=sQuery(id+"F3.wireOp",EDGE,"E2");var subQ2=makeQuery(id+"F3.imprint","INTERSECT",VERTEX,{"derivedFrom":[subQ1,subQ0]});Q24=makeQuery(id+"F3.imprint","IMPRINT",FACE,{"disambiguationData":[TD([[makeQuery(id+"F3.imprint","IMPRINT",EDGE,{"disambiguationData":[TD([[subQ2,-1.0]])],"derivedFrom":subQ1}),-1.0]])]});}
            var Q25;
            {var subQ3=sQuery(id+"F3.wireOp",EDGE,"E69");var subQ5=sQuery(id+"F3.wireOp",EDGE,"E8");var subQ6=makeQuery(id+"F3.imprint","INTERSECT",VERTEX,{"derivedFrom":[subQ5,subQ3]});Q25=makeQuery(id+"F3.imprint","IMPRINT",FACE,{"disambiguationData":[TD([[makeQuery(id+"F3.imprint","IMPRINT",EDGE,{"disambiguationData":[TD([[subQ6,-1.0]])],"derivedFrom":subQ5}),1.0]])]});}
            extrude(context, id + "F6", {"entities" : qUnion([Q0, Q1, Q2, Q3, Q4, Q5, Q6, Q7, Q8, Q9, Q10, Q11, Q12, Q13, Q14, Q15, Q16, Q17, Q18, Q19, Q20, Q21, Q22, Q23, Q24, Q25]), "operationType" : NewBodyOperationType.ADD, "depth" : getVariable(context, 'height') - getVariable(context, 'lvl1_height'), "offsetDistance" : 25 * mm});
        }
        {
            var Q0;
            {var subQ3=sQuery(id+"F3.wireOp",EDGE,"E87");var subQ5=sQuery(id+"F3.wireOp",EDGE,"E9");var subQ6=makeQuery(id+"F3.imprint","INTERSECT",VERTEX,{"derivedFrom":[subQ5,subQ3]});Q0=makeQuery(id+"F3.imprint","IMPRINT",FACE,{"disambiguationData":[TD([[makeQuery(id+"F3.imprint","IMPRINT",EDGE,{"disambiguationData":[TD([[subQ6,-1.0]])],"derivedFrom":subQ5}),1.0]])]});}
            var Q1;
            {var subQ3=sQuery(id+"F3.wireOp",EDGE,"E69");var subQ5=sQuery(id+"F3.wireOp",EDGE,"E8");var subQ6=makeQuery(id+"F3.imprint","INTERSECT",VERTEX,{"derivedFrom":[subQ5,subQ3]});Q1=makeQuery(id+"F3.imprint","IMPRINT",FACE,{"disambiguationData":[TD([[makeQuery(id+"F3.imprint","IMPRINT",EDGE,{"disambiguationData":[TD([[subQ6,-1.0]])],"derivedFrom":subQ5}),1.0]])]});}
            extrude(context, id + "F7", {"entities" : qUnion([Q0, Q1]), "operationType" : NewBodyOperationType.REMOVE, "depth" : getVariable(context, 'lvl2_height'), "offsetDistance" : 25 * mm});
        }
        {
            var Q0;
            Q0=makeQuery(id+"F3.imprint","IMPRINT",FACE,{"disambiguationData":[TD([[makeQuery(id+"F3.imprint","IMPRINT",EDGE,{"derivedFrom":sQuery(id+"F3.wireOp",EDGE,"E30")}),1.0]])]});
            var Q1;
            Q1=makeQuery(id+"F3.imprint","IMPRINT",FACE,{"disambiguationData":[TD([[makeQuery(id+"F3.imprint","IMPRINT",EDGE,{"derivedFrom":sQuery(id+"F3.wireOp",EDGE,"E25.3.0")}),-1.0]])]});
            var Q2;
            Q2=makeQuery(id+"F3.imprint","IMPRINT",FACE,{"disambiguationData":[TD([[makeQuery(id+"F3.imprint","IMPRINT",EDGE,{"derivedFrom":sQuery(id+"F3.wireOp",EDGE,"E24")}),-1.0]])]});
            var Q3;
            Q3=makeQuery(id+"F3.imprint","IMPRINT",FACE,{"disambiguationData":[TD([[makeQuery(id+"F3.imprint","IMPRINT",EDGE,{"derivedFrom":sQuery(id+"F3.wireOp",EDGE,"E25.1.0")}),-1.0]])]});
            var Q4;
            Q4=makeQuery(id+"F3.imprint","IMPRINT",FACE,{"disambiguationData":[TD([[makeQuery(id+"F3.imprint","IMPRINT",EDGE,{"derivedFrom":sQuery(id+"F3.wireOp",EDGE,"E25.2.0")}),-1.0]])]});
            var Q5;
            {var subQ0=sQuery(id+"F3.wireOp",EDGE,"E15.2.0");var subQ1=sQuery(id+"F3.wireOp",EDGE,"E4");var subQ2=makeQuery(id+"F3.imprint","INTERSECT",VERTEX,{"derivedFrom":[subQ1,subQ0]});Q5=makeQuery(id+"F3.imprint","IMPRINT",FACE,{"disambiguationData":[TD([[makeQuery(id+"F3.imprint","IMPRINT",EDGE,{"disambiguationData":[TD([[subQ2,-1.0]])],"derivedFrom":subQ1}),-1.0]])]});}
            var Q6;
            {var subQ0=sQuery(id+"F3.wireOp",EDGE,"E2");var subQ5=makeQuery(id+"F3.imprint","INTERSECT",VERTEX,{"derivedFrom":[subQ0,sQuery(id+"F3.wireOp",EDGE,"E12")]});Q6=makeQuery(id+"F3.imprint","IMPRINT",FACE,{"disambiguationData":[TD([[makeQuery(id+"F3.imprint","IMPRINT",EDGE,{"disambiguationData":[TD([[subQ5,-1.0]])],"derivedFrom":subQ0}),1.0]])]});}
            var Q7;
            {var subQ0=sQuery(id+"F3.wireOp",EDGE,"E14.MirrorCS");var subQ1=sQuery(id+"F3.wireOp",EDGE,"E4");var subQ2=makeQuery(id+"F3.imprint","INTERSECT",VERTEX,{"derivedFrom":[subQ1,subQ0]});Q7=makeQuery(id+"F3.imprint","IMPRINT",FACE,{"disambiguationData":[TD([[makeQuery(id+"F3.imprint","IMPRINT",EDGE,{"disambiguationData":[TD([[subQ2,1.0]])],"derivedFrom":subQ1}),-1.0]])]});}
            var Q8;
            {var subQ0=sQuery(id+"F3.wireOp",EDGE,"E15.1.0");var subQ1=sQuery(id+"F3.wireOp",EDGE,"E4");var subQ2=makeQuery(id+"F3.imprint","INTERSECT",VERTEX,{"derivedFrom":[subQ1,subQ0]});Q8=makeQuery(id+"F3.imprint","IMPRINT",FACE,{"disambiguationData":[TD([[makeQuery(id+"F3.imprint","IMPRINT",EDGE,{"disambiguationData":[TD([[subQ2,-1.0]])],"derivedFrom":subQ1}),-1.0]])]});}
            var Q9;
            {var subQ0=sQuery(id+"F3.wireOp",EDGE,"E69");var subQ1=sQuery(id+"F3.wireOp",EDGE,"E8");var subQ2=makeQuery(id+"F3.imprint","INTERSECT",VERTEX,{"derivedFrom":[subQ1,subQ0]});Q9=makeQuery(id+"F3.imprint","IMPRINT",FACE,{"disambiguationData":[TD([[makeQuery(id+"F3.imprint","IMPRINT",EDGE,{"disambiguationData":[TD([[subQ2,-1.0]])],"derivedFrom":subQ1}),-1.0]])]});}
            var Q10;
            {var subQ4=sQuery(id+"F3.wireOp",EDGE,"E6");var subQ5=makeQuery(id+"F3.imprint","INTERSECT",VERTEX,{"derivedFrom":[subQ4,sQuery(id+"F3.wireOp",EDGE,"E12")]});Q10=makeQuery(id+"F3.imprint","IMPRINT",FACE,{"disambiguationData":[TD([[makeQuery(id+"F3.imprint","IMPRINT",EDGE,{"disambiguationData":[TD([[subQ5,-1.0]])],"derivedFrom":subQ4}),-1.0]])]});}
            var Q11;
            {var subQ3=sQuery(id+"F3.wireOp",EDGE,"E69");var subQ5=sQuery(id+"F3.wireOp",EDGE,"E8");var subQ6=makeQuery(id+"F3.imprint","INTERSECT",VERTEX,{"derivedFrom":[subQ5,subQ3]});Q11=makeQuery(id+"F3.imprint","IMPRINT",FACE,{"disambiguationData":[TD([[makeQuery(id+"F3.imprint","IMPRINT",EDGE,{"disambiguationData":[TD([[subQ6,-1.0]])],"derivedFrom":subQ5}),1.0]])]});}
            var Q12;
            {var subQ0=sQuery(id+"F3.wireOp",EDGE,"E15.1.0");var subQ1=sQuery(id+"F3.wireOp",EDGE,"E2");var subQ2=makeQuery(id+"F3.imprint","INTERSECT",VERTEX,{"derivedFrom":[subQ1,subQ0]});Q12=makeQuery(id+"F3.imprint","IMPRINT",FACE,{"disambiguationData":[TD([[makeQuery(id+"F3.imprint","IMPRINT",EDGE,{"disambiguationData":[TD([[subQ2,-1.0]])],"derivedFrom":subQ1}),-1.0]])]});}
            var Q13;
            {var subQ0=sQuery(id+"F3.wireOp",EDGE,"E12");var subQ1=sQuery(id+"F3.wireOp",EDGE,"E2");var subQ2=makeQuery(id+"F3.imprint","INTERSECT",VERTEX,{"derivedFrom":[subQ1,subQ0]});Q13=makeQuery(id+"F3.imprint","IMPRINT",FACE,{"disambiguationData":[TD([[makeQuery(id+"F3.imprint","IMPRINT",EDGE,{"disambiguationData":[TD([[subQ2,1.0]])],"derivedFrom":subQ1}),-1.0]])]});}
            var Q14;
            {var subQ0=sQuery(id+"F3.wireOp",EDGE,"E12");var subQ1=sQuery(id+"F3.wireOp",EDGE,"E2");var subQ2=makeQuery(id+"F3.imprint","INTERSECT",VERTEX,{"derivedFrom":[subQ1,subQ0]});Q14=makeQuery(id+"F3.imprint","IMPRINT",FACE,{"disambiguationData":[TD([[makeQuery(id+"F3.imprint","IMPRINT",EDGE,{"disambiguationData":[TD([[subQ2,-1.0]])],"derivedFrom":subQ1}),-1.0]])]});}
            var Q15;
            {var subQ0=sQuery(id+"F3.wireOp",EDGE,"E14.MirrorCS");var subQ1=sQuery(id+"F3.wireOp",EDGE,"E2");var subQ2=makeQuery(id+"F3.imprint","INTERSECT",VERTEX,{"derivedFrom":[subQ1,subQ0]});Q15=makeQuery(id+"F3.imprint","IMPRINT",FACE,{"disambiguationData":[TD([[makeQuery(id+"F3.imprint","IMPRINT",EDGE,{"disambiguationData":[TD([[subQ2,-1.0]])],"derivedFrom":subQ1}),-1.0]])]});}
            var Q16;
            {var subQ0=sQuery(id+"F3.wireOp",EDGE,"E15.2.0");var subQ1=sQuery(id+"F3.wireOp",EDGE,"E2");var subQ2=makeQuery(id+"F3.imprint","INTERSECT",VERTEX,{"derivedFrom":[subQ1,subQ0]});Q16=makeQuery(id+"F3.imprint","IMPRINT",FACE,{"disambiguationData":[TD([[makeQuery(id+"F3.imprint","IMPRINT",EDGE,{"disambiguationData":[TD([[subQ2,-1.0]])],"derivedFrom":subQ1}),-1.0]])]});}
            var Q17;
            {var subQ0=sQuery(id+"F3.wireOp",EDGE,"E15.1.1");var subQ1=sQuery(id+"F3.wireOp",EDGE,"E2");var subQ2=makeQuery(id+"F3.imprint","INTERSECT",VERTEX,{"derivedFrom":[subQ1,subQ0]});Q17=makeQuery(id+"F3.imprint","IMPRINT",FACE,{"disambiguationData":[TD([[makeQuery(id+"F3.imprint","IMPRINT",EDGE,{"disambiguationData":[TD([[subQ2,-1.0]])],"derivedFrom":subQ1}),-1.0]])]});}
            var Q18;
            {var subQ0=sQuery(id+"F3.wireOp",EDGE,"E21.2.0");var subQ1=sQuery(id+"F3.wireOp",EDGE,"E5");var subQ2=makeQuery(id+"F3.imprint","INTERSECT",VERTEX,{"derivedFrom":[subQ1,subQ0]});Q18=makeQuery(id+"F3.imprint","IMPRINT",FACE,{"disambiguationData":[TD([[makeQuery(id+"F3.imprint","IMPRINT",EDGE,{"disambiguationData":[TD([[subQ2,-1.0]])],"derivedFrom":subQ1}),-1.0]])]});}
            var Q19;
            Q19=makeQuery(id+"F3.imprint","IMPRINT",FACE,{"disambiguationData":[TD([[makeQuery(id+"F3.imprint","IMPRINT",EDGE,{"derivedFrom":sQuery(id+"F3.wireOp",EDGE,"E29.3.0")}),-1.0]])]});
            var Q20;
            Q20=makeQuery(id+"F3.imprint","IMPRINT",FACE,{"disambiguationData":[TD([[makeQuery(id+"F3.imprint","IMPRINT",EDGE,{"derivedFrom":sQuery(id+"F3.wireOp",EDGE,"E42")}),1.0]])]});
            var Q21;
            Q21=makeQuery(id+"F3.imprint","IMPRINT",FACE,{"disambiguationData":[TD([[makeQuery(id+"F3.imprint","IMPRINT",EDGE,{"derivedFrom":sQuery(id+"F3.wireOp",EDGE,"E28")}),-1.0]])]});
            var Q22;
            Q22=makeQuery(id+"F3.imprint","IMPRINT",FACE,{"disambiguationData":[TD([[makeQuery(id+"F3.imprint","IMPRINT",EDGE,{"derivedFrom":sQuery(id+"F3.wireOp",EDGE,"E29.1.0")}),-1.0]])]});
            var Q23;
            Q23=makeQuery(id+"F3.imprint","IMPRINT",FACE,{"disambiguationData":[TD([[makeQuery(id+"F3.imprint","IMPRINT",EDGE,{"derivedFrom":sQuery(id+"F3.wireOp",EDGE,"E29.2.0")}),-1.0]])]});
            var Q24;
            {var subQ0=sQuery(id+"F3.wireOp",EDGE,"E87");var subQ1=sQuery(id+"F3.wireOp",EDGE,"E9");var subQ2=makeQuery(id+"F3.imprint","INTERSECT",VERTEX,{"derivedFrom":[subQ1,subQ0]});Q24=makeQuery(id+"F3.imprint","IMPRINT",FACE,{"disambiguationData":[TD([[makeQuery(id+"F3.imprint","IMPRINT",EDGE,{"disambiguationData":[TD([[subQ2,-1.0]])],"derivedFrom":subQ1}),-1.0]])]});}
            var Q25;
            {var subQ7=sQuery(id+"F3.wireOp",EDGE,"E7");var subQ8=makeQuery(id+"F3.imprint","INTERSECT",VERTEX,{"derivedFrom":[subQ7,sQuery(id+"F3.wireOp",EDGE,"E18")]});Q25=makeQuery(id+"F3.imprint","IMPRINT",FACE,{"disambiguationData":[TD([[makeQuery(id+"F3.imprint","IMPRINT",EDGE,{"disambiguationData":[TD([[subQ8,-1.0]])],"derivedFrom":subQ7}),-1.0]])]});}
            var Q26;
            {var subQ3=sQuery(id+"F3.wireOp",EDGE,"E87");var subQ5=sQuery(id+"F3.wireOp",EDGE,"E9");var subQ6=makeQuery(id+"F3.imprint","INTERSECT",VERTEX,{"derivedFrom":[subQ5,subQ3]});Q26=makeQuery(id+"F3.imprint","IMPRINT",FACE,{"disambiguationData":[TD([[makeQuery(id+"F3.imprint","IMPRINT",EDGE,{"disambiguationData":[TD([[subQ6,-1.0]])],"derivedFrom":subQ5}),1.0]])]});}
            var Q27;
            {var subQ0=sQuery(id+"F3.wireOp",EDGE,"E20.MirrorCS");var subQ1=sQuery(id+"F3.wireOp",EDGE,"E5");var subQ2=makeQuery(id+"F3.imprint","INTERSECT",VERTEX,{"derivedFrom":[subQ1,subQ0]});Q27=makeQuery(id+"F3.imprint","IMPRINT",FACE,{"disambiguationData":[TD([[makeQuery(id+"F3.imprint","IMPRINT",EDGE,{"disambiguationData":[TD([[subQ2,1.0]])],"derivedFrom":subQ1}),-1.0]])]});}
            var Q28;
            {var subQ0=sQuery(id+"F3.wireOp",EDGE,"E21.2.0");var subQ1=sQuery(id+"F3.wireOp",EDGE,"E3");var subQ2=makeQuery(id+"F3.imprint","INTERSECT",VERTEX,{"derivedFrom":[subQ1,subQ0]});Q28=makeQuery(id+"F3.imprint","IMPRINT",FACE,{"disambiguationData":[TD([[makeQuery(id+"F3.imprint","IMPRINT",EDGE,{"disambiguationData":[TD([[subQ2,-1.0]])],"derivedFrom":subQ1}),-1.0]])]});}
            var Q29;
            {var subQ0=sQuery(id+"F3.wireOp",EDGE,"E18");var subQ1=sQuery(id+"F3.wireOp",EDGE,"E3");var subQ2=makeQuery(id+"F3.imprint","INTERSECT",VERTEX,{"derivedFrom":[subQ1,subQ0]});Q29=makeQuery(id+"F3.imprint","IMPRINT",FACE,{"disambiguationData":[TD([[makeQuery(id+"F3.imprint","IMPRINT",EDGE,{"disambiguationData":[TD([[subQ2,-1.0]])],"derivedFrom":subQ1}),-1.0]])]});}
            var Q30;
            {var subQ0=sQuery(id+"F3.wireOp",EDGE,"E21.1.0");var subQ1=sQuery(id+"F3.wireOp",EDGE,"E5");var subQ2=makeQuery(id+"F3.imprint","INTERSECT",VERTEX,{"derivedFrom":[subQ1,subQ0]});Q30=makeQuery(id+"F3.imprint","IMPRINT",FACE,{"disambiguationData":[TD([[makeQuery(id+"F3.imprint","IMPRINT",EDGE,{"disambiguationData":[TD([[subQ2,-1.0]])],"derivedFrom":subQ1}),-1.0]])]});}
            var Q31;
            {var subQ0=sQuery(id+"F3.wireOp",EDGE,"E21.1.0");var subQ1=sQuery(id+"F3.wireOp",EDGE,"E3");var subQ2=makeQuery(id+"F3.imprint","INTERSECT",VERTEX,{"derivedFrom":[subQ1,subQ0]});Q31=makeQuery(id+"F3.imprint","IMPRINT",FACE,{"disambiguationData":[TD([[makeQuery(id+"F3.imprint","IMPRINT",EDGE,{"disambiguationData":[TD([[subQ2,-1.0]])],"derivedFrom":subQ1}),-1.0]])]});}
            var Q32;
            {var subQ0=sQuery(id+"F3.wireOp",EDGE,"E3");var subQ5=makeQuery(id+"F3.imprint","INTERSECT",VERTEX,{"derivedFrom":[subQ0,sQuery(id+"F3.wireOp",EDGE,"E18")]});Q32=makeQuery(id+"F3.imprint","IMPRINT",FACE,{"disambiguationData":[TD([[makeQuery(id+"F3.imprint","IMPRINT",EDGE,{"disambiguationData":[TD([[subQ5,-1.0]])],"derivedFrom":subQ0}),1.0]])]});}
            var Q33;
            {var subQ0=sQuery(id+"F3.wireOp",EDGE,"E20.MirrorCS");var subQ1=sQuery(id+"F3.wireOp",EDGE,"E3");var subQ2=makeQuery(id+"F3.imprint","INTERSECT",VERTEX,{"derivedFrom":[subQ1,subQ0]});Q33=makeQuery(id+"F3.imprint","IMPRINT",FACE,{"disambiguationData":[TD([[makeQuery(id+"F3.imprint","IMPRINT",EDGE,{"disambiguationData":[TD([[subQ2,-1.0]])],"derivedFrom":subQ1}),-1.0]])]});}
            var Q34;
            {var subQ0=sQuery(id+"F3.wireOp",EDGE,"E18");var subQ1=sQuery(id+"F3.wireOp",EDGE,"E3");var subQ2=makeQuery(id+"F3.imprint","INTERSECT",VERTEX,{"derivedFrom":[subQ1,subQ0]});Q34=makeQuery(id+"F3.imprint","IMPRINT",FACE,{"disambiguationData":[TD([[makeQuery(id+"F3.imprint","IMPRINT",EDGE,{"disambiguationData":[TD([[subQ2,1.0]])],"derivedFrom":subQ1}),-1.0]])]});}
            var Q35;
            {var subQ0=sQuery(id+"F3.wireOp",EDGE,"E21.1.1");var subQ1=sQuery(id+"F3.wireOp",EDGE,"E3");var subQ2=makeQuery(id+"F3.imprint","INTERSECT",VERTEX,{"derivedFrom":[subQ1,subQ0]});Q35=makeQuery(id+"F3.imprint","IMPRINT",FACE,{"disambiguationData":[TD([[makeQuery(id+"F3.imprint","IMPRINT",EDGE,{"disambiguationData":[TD([[subQ2,-1.0]])],"derivedFrom":subQ1}),-1.0]])]});}
            extrude(context, id + "F8", {"entities" : qUnion([Q0, Q1, Q2, Q3, Q4, Q5, Q6, Q7, Q8, Q9, Q10, Q11, Q12, Q13, Q14, Q15, Q16, Q17, Q18, Q19, Q20, Q21, Q22, Q23, Q24, Q25, Q26, Q27, Q28, Q29, Q30, Q31, Q32, Q33, Q34, Q35]), "depth" : 2 * mm, "offsetDistance" : 25 * mm});
        }
    });
